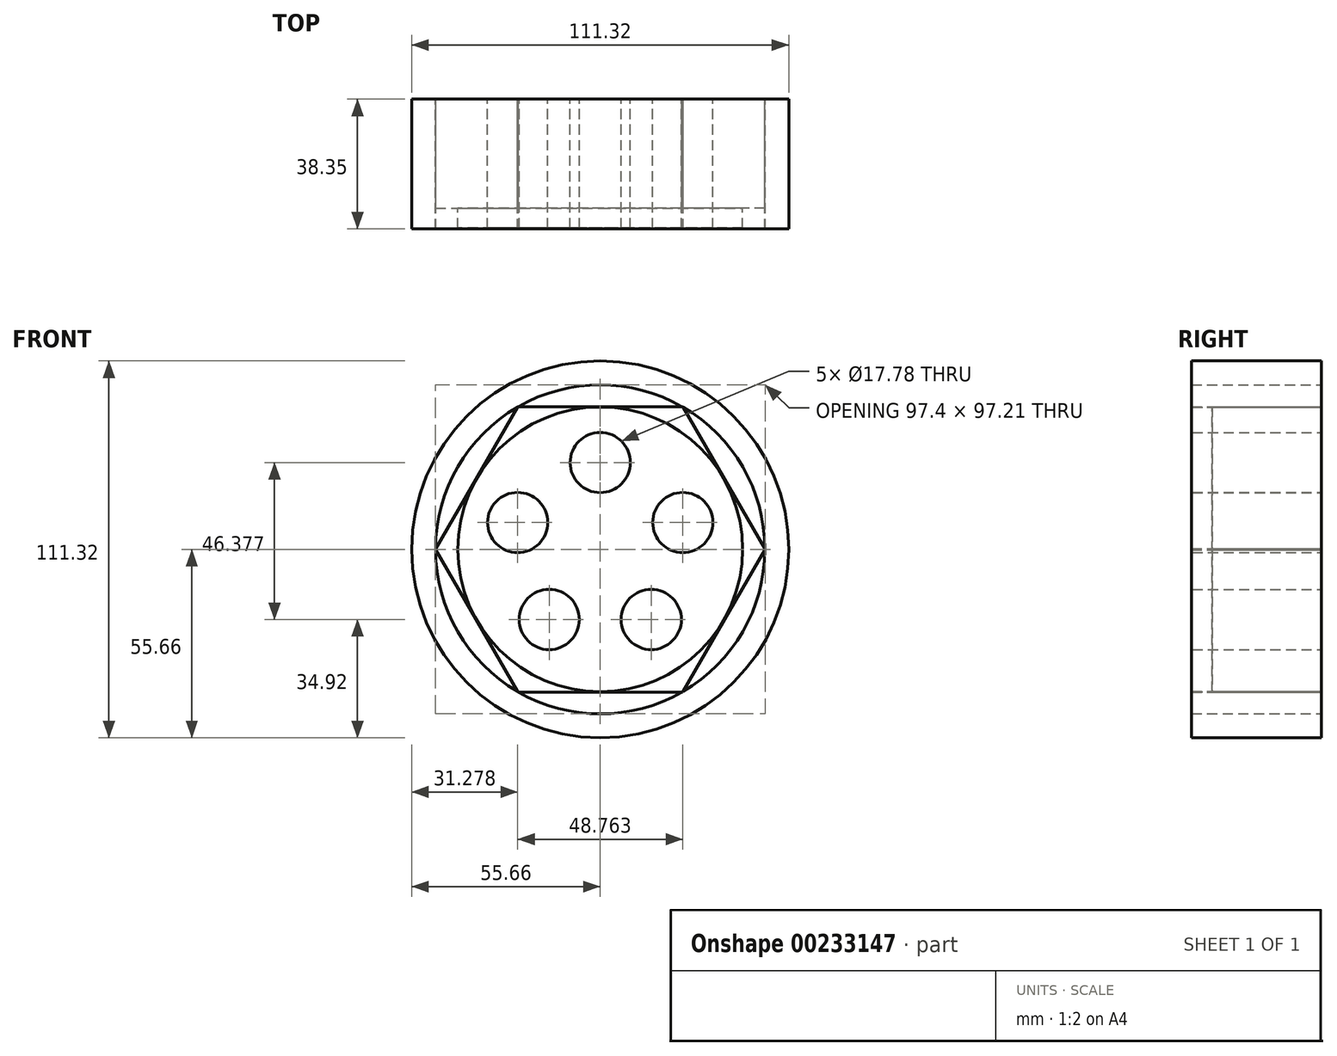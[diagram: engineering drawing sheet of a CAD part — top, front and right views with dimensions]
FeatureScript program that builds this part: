
annotation { "Feature Type Name" : "Feature", "Feature Type Description" : "" }
export const myFeature = defineFeature(function(context is Context, id is Id, definition is map)
    precondition{}
    {
        {
            var Q0;
            Q0=qCreatedBy(makeId("Front.planeOp"),FACE);
            var sketch = newSketch(context, id + "F0", { "sketchPlane" : qUnion([Q0])});
            skCircle(sketch, "E0", {"center": v(0, 0) * mm, "radius": 55.66 * mm});
            skCircle(sketch, "E1", {"center": v(0, 0) * mm, "radius": 48.6 * mm});
            skCircle(sketch, "E2.cCircle", {"center": v(0, 0) * mm, "radius": 42.18 * mm, "construction": true});
            skLineSegment(sketch, "E2.0", {"start": v(-24.35, 42.18) * mm, "end": v(24.35, 42.18) * mm});
            skLineSegment(sketch, "E2.1", {"start": v(24.35, 42.18) * mm, "end": v(48.7, 0) * mm});
            skLineSegment(sketch, "E2.2", {"start": v(48.7, 0) * mm, "end": v(24.35, -42.18) * mm});
            skLineSegment(sketch, "E2.3", {"start": v(24.35, -42.18) * mm, "end": v(-24.35, -42.18) * mm});
            skLineSegment(sketch, "E2.4", {"start": v(-24.35, -42.18) * mm, "end": v(-48.7, 0) * mm});
            skLineSegment(sketch, "E2.5", {"start": v(-48.7, 0) * mm, "end": v(-24.35, 42.18) * mm});
            skPoint(sketch, "E2.0.midPoint", {"position": v(0, 42.18) * mm});
            skCircle(sketch, "E3", {"center": v(0, 0) * mm, "radius": 42.05 * mm});
            skCircle(sketch, "E4", {"center": v(0, 25.64) * mm, "radius": 8.9 * mm});
            skCircle(sketch, "E5.1.0", {"center": v(-24.38, 7.92) * mm, "radius": 8.9 * mm});
            skCircle(sketch, "E5.2.0", {"center": v(-15.07, -20.74) * mm, "radius": 8.9 * mm});
            skCircle(sketch, "E5.3.0", {"center": v(15.07, -20.74) * mm, "radius": 8.9 * mm});
            skCircle(sketch, "E5.4.0", {"center": v(24.38, 7.92) * mm, "radius": 8.9 * mm});
            skSolve(sketch);
        }
        {
            var Q0;
            Q0 = qSketchRegion(id + "F0", true);
            extrude(context, id + "F1", {"entities" : qUnion([Q0]), "depth" : 38.35 * mm});
        }
        {
            var Q0;
            Q0=makeQuery(id+"F0.imprint","IMPRINT",FACE,{"disambiguationData":[TD([[makeQuery(id+"F0.imprint","IMPRINT",EDGE,{"derivedFrom":sQuery(id+"F0.wireOp",EDGE,"E3")}),1.0]])]});
            extrude(context, id + "F2", {"entities" : qUnion([Q0]), "depth" : 38.1 * mm});
        }
        {
            var Q0;
            Q0=makeQuery(id+"F0.imprint","IMPRINT",FACE,{"disambiguationData":[TD([[makeQuery(id+"F0.imprint","IMPRINT",EDGE,{"derivedFrom":sQuery(id+"F0.wireOp",EDGE,"E3")}),-1.0]])]});
            extrude(context, id + "F3", {"entities" : qUnion([Q0]), "operationType" : NewBodyOperationType.ADD, "depth" : 32.26 * mm});
        }
    });
